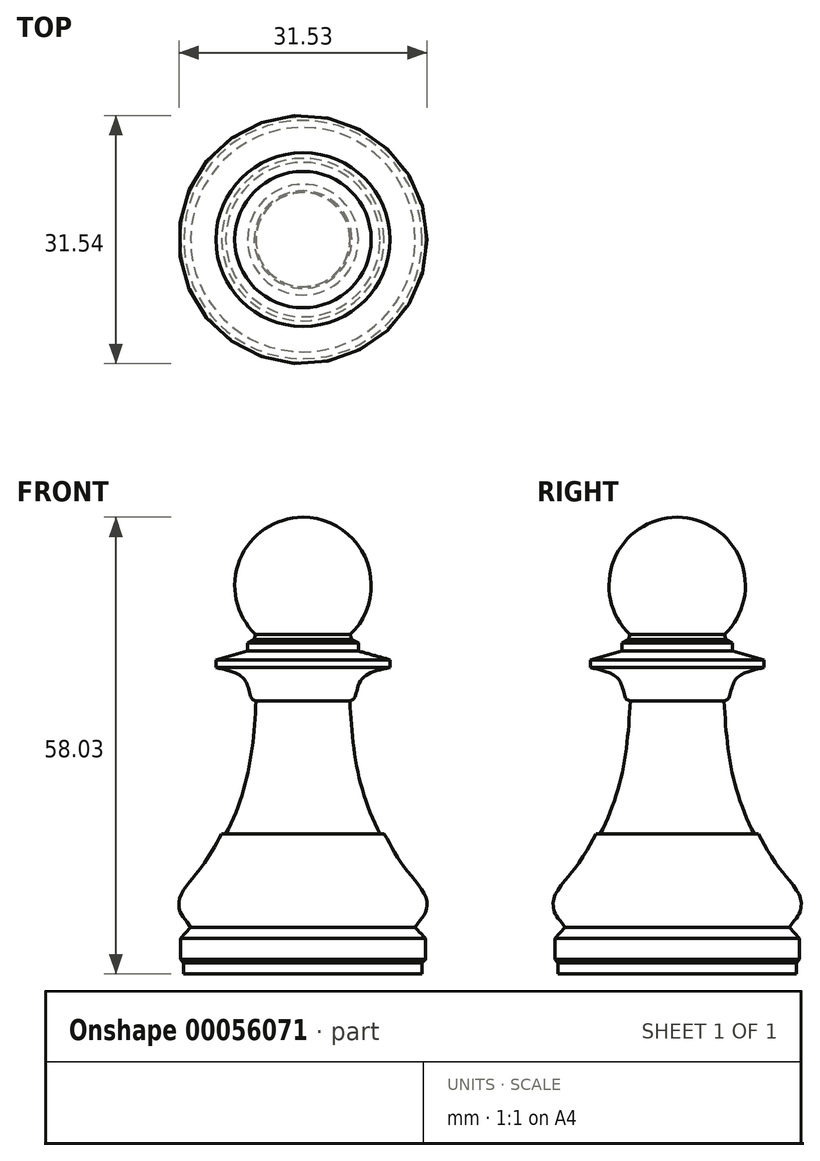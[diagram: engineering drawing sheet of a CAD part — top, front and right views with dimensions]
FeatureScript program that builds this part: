
annotation { "Feature Type Name" : "Feature", "Feature Type Description" : "" }
export const myFeature = defineFeature(function(context is Context, id is Id, definition is map)
    precondition{}
    {
        {
            var Q0;
            Q0=qCreatedBy(makeId("Front.planeOp"),FACE);
            var sketch = newSketch(context, id + "F0", { "sketchPlane" : qUnion([Q0])});
            skLineSegment(sketch, "E0", {"start": v(0, 59.85) * mm, "end": v(0, -47.74) * mm, "construction": true});
            skArc(sketch, "E1", {"start": v(6, 17.04) * mm, "mid": v(8.03, 26.52) * mm, "end": v(0, 31.94) * mm});
            skLineSegment(sketch, "E2", {"start": v(6, 17.04) * mm, "end": v(6.2, 16.4) * mm});
            skLineSegment(sketch, "E3", {"start": v(6.2, 16.4) * mm, "end": v(7.04, 16) * mm});
            skLineSegment(sketch, "E4", {"start": v(7.04, 16) * mm, "end": v(7.04, 14.94) * mm});
            skLineSegment(sketch, "E5", {"start": v(7.04, 14.94) * mm, "end": v(11.05, 13.83) * mm});
            skLineSegment(sketch, "E6", {"start": v(11.05, 13.83) * mm, "end": v(11.05, 12.83) * mm});
            skFitSpline(sketch, "E7", {"points": [v(11.05, 12.83) * mm, v(7.42, 11.3) * mm, v(6.52, 8.95) * mm, v(5.96, 8.62) * mm], "startDerivative": vector(-9.72, -1.96) * mm, "endDerivative": vector(-3.38, -0.81) * mm});
            skFitSpline(sketch, "E8", {"points": [v(5.96, 8.62) * mm, v(6.88, 0) * mm, v(9.8, -8.3) * mm], "startDerivative": vector(0.98, -17.43) * mm, "endDerivative": vector(8.02, -15.21) * mm});
            skLineSegment(sketch, "E9", {"start": v(9.8, -8.3) * mm, "end": v(10.32, -8.3) * mm});
            skFitSpline(sketch, "E10", {"points": [v(10.32, -8.3) * mm, v(12.78, -12.37) * mm, v(15.58, -16.24) * mm, v(15.51, -18.38) * mm, v(14.26, -20.17) * mm], "startDerivative": vector(7.79, -12.88) * mm, "endDerivative": vector(-7.64, -12.47) * mm});
            skLineSegment(sketch, "E11", {"start": v(14.26, -20.17) * mm, "end": v(15.55, -21.55) * mm});
            skLineSegment(sketch, "E12", {"start": v(15.55, -21.55) * mm, "end": v(15.55, -24.25) * mm});
            skLineSegment(sketch, "E13", {"start": v(15.55, -24.25) * mm, "end": v(15.13, -24.67) * mm});
            skLineSegment(sketch, "E14", {"start": v(15.13, -24.67) * mm, "end": v(15.13, -26.1) * mm});
            skLineSegment(sketch, "E15", {"start": v(15.13, -26.1) * mm, "end": v(0, -26.1) * mm});
            skLineSegment(sketch, "E16", {"start": v(0, 31.94) * mm, "end": v(0, -26.1) * mm});
            skSolve(sketch);
        }
        {
            var Q0;
            Q0=makeQuery(id+"F0.imprint","IMPRINT",FACE,{"disambiguationData":[TD([[makeQuery(id+"F0.imprint","IMPRINT",EDGE,{"derivedFrom":sQuery(id+"F0.wireOp",EDGE,"E1")}),1.0]])]});
            var Q1;
            Q1=sQuery(id+"F0.wireOp",EDGE,"E0");
            revolve(context, id + "F1", {"entities" : qUnion([Q0]), "axis" : qUnion([Q1]), "revolveType" : RevolveType.FULL});
        }
    });
